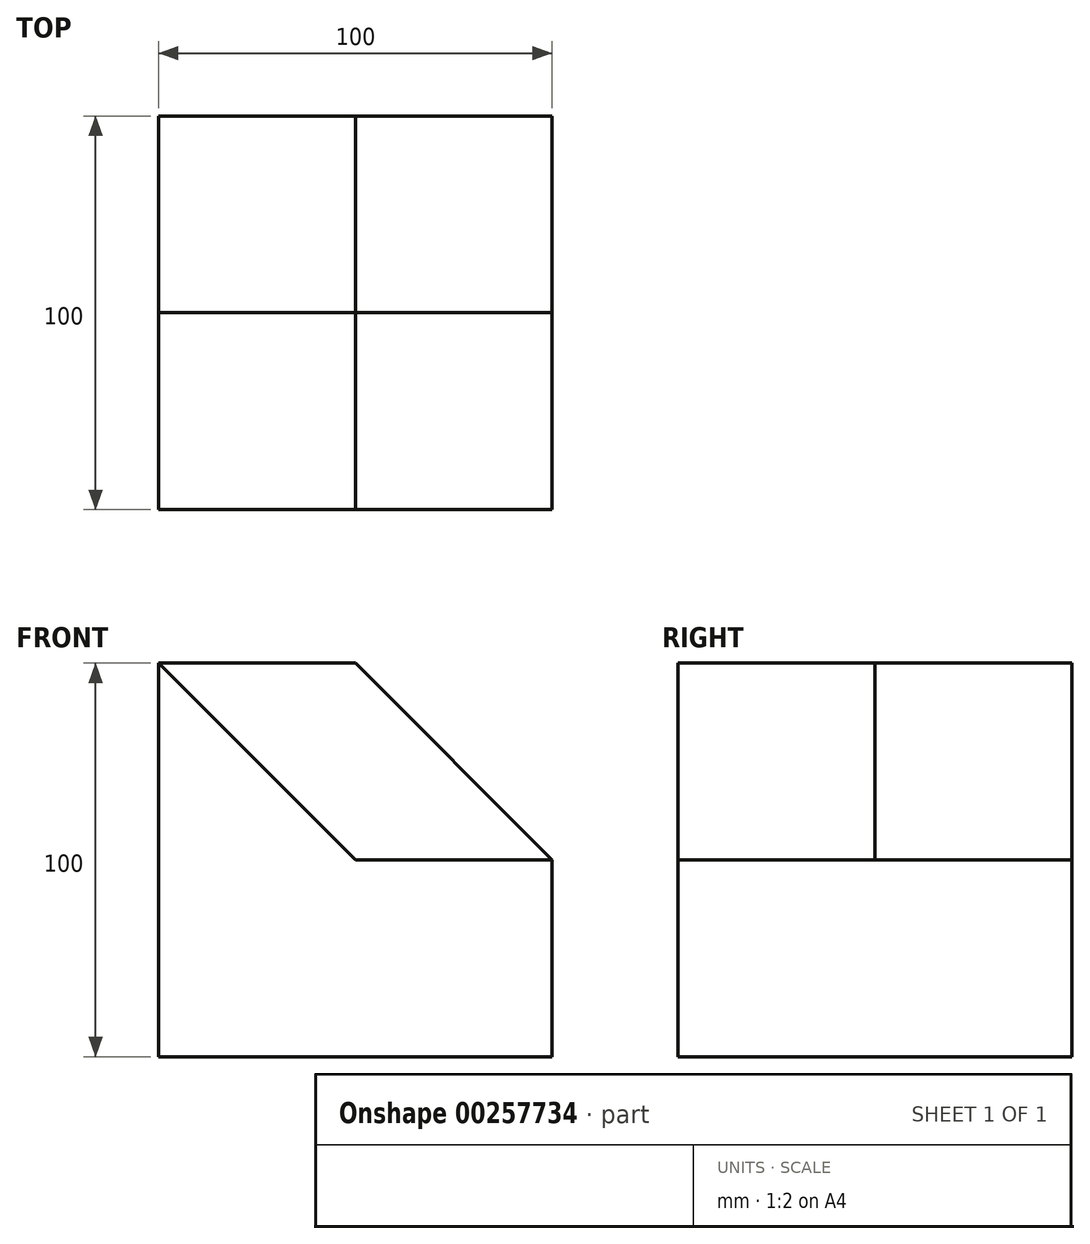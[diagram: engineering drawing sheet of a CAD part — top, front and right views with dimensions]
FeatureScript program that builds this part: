
annotation { "Feature Type Name" : "Feature", "Feature Type Description" : "" }
export const myFeature = defineFeature(function(context is Context, id is Id, definition is map)
    precondition{}
    {
        {
            var Q0;
            Q0=qCreatedBy(makeId("Front.planeOp"),FACE);
            var sketch = newSketch(context, id + "F0", { "sketchPlane" : qUnion([Q0])});
            skLineSegment(sketch, "E0", {"start": v(0, 0) * mm, "end": v(0, 50) * mm});
            skLineSegment(sketch, "E1", {"start": v(0, 50) * mm, "end": v(-50, 100) * mm});
            skLineSegment(sketch, "E2", {"start": v(-50, 100) * mm, "end": v(-100, 100) * mm});
            skLineSegment(sketch, "E3", {"start": v(-100, 100) * mm, "end": v(-100, 0) * mm});
            skLineSegment(sketch, "E4", {"start": v(-100, 0) * mm, "end": v(0, 0) * mm});
            skSolve(sketch);
        }
        {
            var Q0;
            Q0 = qSketchRegion(id + "F0", true);
            extrude(context, id + "F1", {"entities" : qUnion([Q0]), "depth" : 100 * mm});
        }
        {
            var Q0;
            Q0=makeQuery(id+"F1.opExtrude","CAP_FACE",FACE,{"disambiguationData":[OSD([sQuery(id+"F0.wireOp",EDGE,"E0"),sQuery(id+"F0.wireOp",EDGE,"E1"),sQuery(id+"F0.wireOp",EDGE,"E2"),sQuery(id+"F0.wireOp",EDGE,"E3"),sQuery(id+"F0.wireOp",EDGE,"E4")])],"isStart":false});
            var sketch = newSketch(context, id + "F2", { "sketchPlane" : qUnion([Q0])});
            skLineSegment(sketch, "E5", {"start": v(0, 50) * mm, "end": v(-50, 50) * mm});
            skLineSegment(sketch, "E6", {"start": v(-50, 50) * mm, "end": v(-100, 100) * mm});
            skLineSegment(sketch, "E7", {"start": v(-100, 100) * mm, "end": v(-50, 100) * mm});
            skLineSegment(sketch, "E8", {"start": v(-50, 100) * mm, "end": v(0, 50) * mm});
            skSolve(sketch);
        }
        {
            var Q0;
            Q0=makeQuery(id+"F2.imprint","IMPRINT",FACE,{"disambiguationData":[TD([[makeQuery(id+"F2.imprint","IMPRINT",EDGE,{"derivedFrom":sQuery(id+"F2.wireOp",EDGE,"E5")}),-1.0]])]});
            extrude(context, id + "F3", {"entities" : qUnion([Q0]), "operationType" : NewBodyOperationType.REMOVE, "oppositeDirection" : true, "depth" : 50 * mm});
        }
    });
